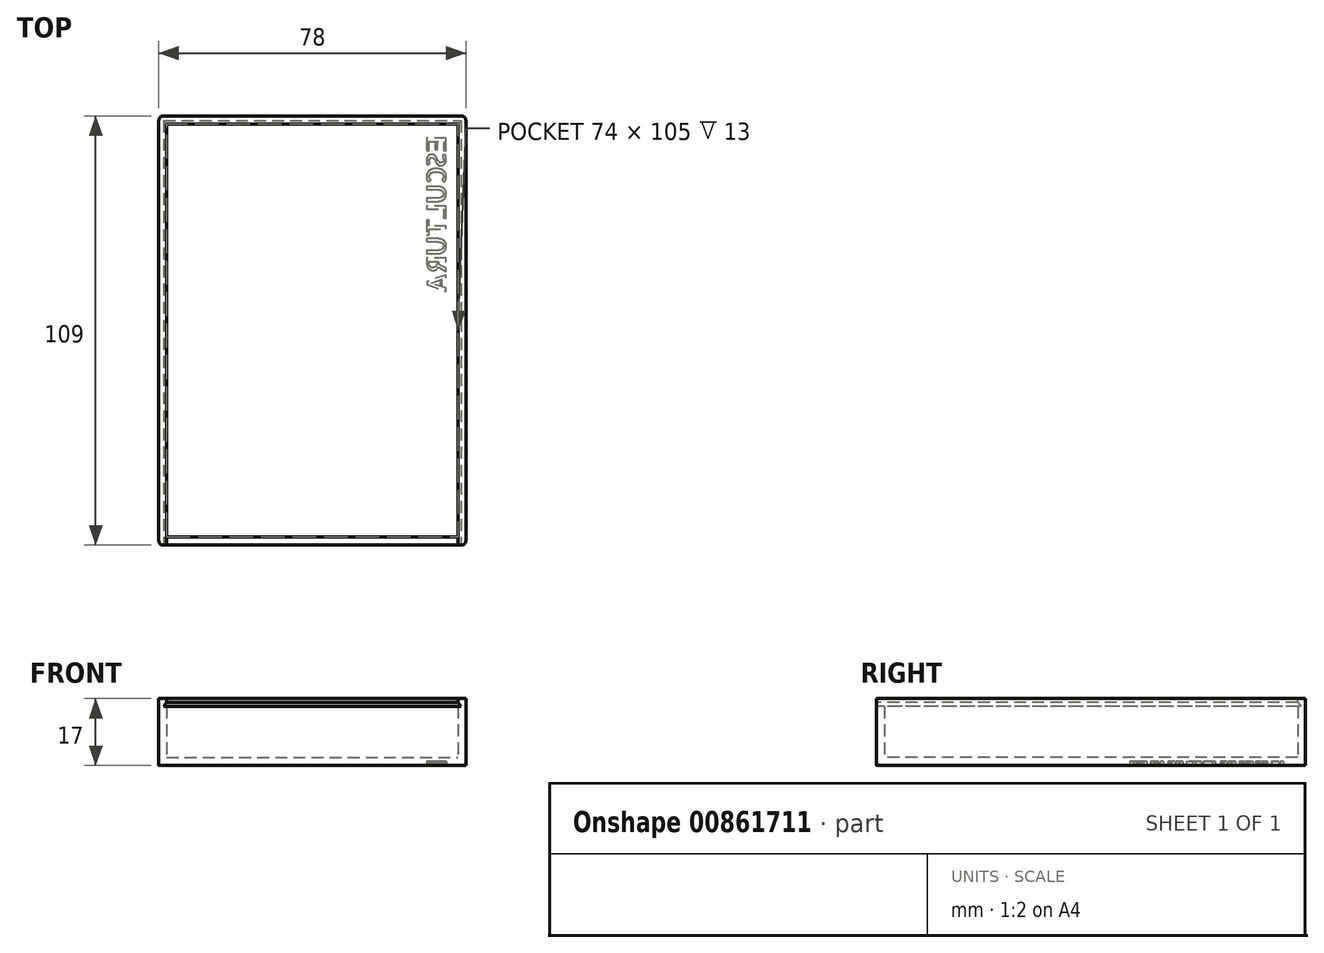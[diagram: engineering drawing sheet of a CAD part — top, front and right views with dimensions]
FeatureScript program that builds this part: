
annotation { "Feature Type Name" : "Feature", "Feature Type Description" : "" }
export const myFeature = defineFeature(function(context is Context, id is Id, definition is map)
    precondition{}
    {
        {
            var Q0;
            Q0=qCreatedBy(makeId("Front.planeOp"),FACE);
            var sketch = newSketch(context, id + "F0", { "sketchPlane" : qUnion([Q0])});
            skLineSegment(sketch, "E0.bottom", {"start": v(0, 0) * mm, "end": v(78, 0) * mm});
            skLineSegment(sketch, "E0.top", {"start": v(0, -15) * mm, "end": v(78, -15) * mm});
            skLineSegment(sketch, "E0.left", {"start": v(0, 0) * mm, "end": v(0, -15) * mm});
            skLineSegment(sketch, "E0.right", {"start": v(78, 0) * mm, "end": v(78, -15) * mm});
            skSolve(sketch);
        }
        {
            var Q0;
            Q0=qSketchRegion(id+"F0",true);
            extrude(context, id + "F1", {"entities" : qUnion([Q0]), "oppositeDirection" : true, "depth" : 109 * mm, "offsetDistance" : 25 * mm});
        }
        {
            var Q0;
            Q0=makeQuery(id+"F1.opExtrude","SWEPT_FACE",FACE,{"disambiguationData":[OSD([sQuery(id+"F0.wireOp",EDGE,"E0.bottom")])]});
            shell(context, id + "F2", {"entities" : qUnion([Q0]), "thickness" : 2 * mm});
        }
        {
            var Q0;
            Q0=makeQuery(id+"F1.opExtrude","CAP_FACE",FACE,{"disambiguationData":[OSD([sQuery(id+"F0.wireOp",EDGE,"E0.bottom"),sQuery(id+"F0.wireOp",EDGE,"E0.top"),sQuery(id+"F0.wireOp",EDGE,"E0.left"),sQuery(id+"F0.wireOp",EDGE,"E0.right")])],"isStart":true});
            var sketch = newSketch(context, id + "F3", { "sketchPlane" : qUnion([Q0])});
            skLineSegment(sketch, "E1", {"start": v(0, 0) * mm, "end": v(0, 2) * mm});
            skLineSegment(sketch, "E2", {"start": v(0, 2) * mm, "end": v(2, 2) * mm});
            skLineSegment(sketch, "E3", {"start": v(2, 2) * mm, "end": v(2, 1) * mm});
            skLineSegment(sketch, "E4", {"start": v(1.2, 0) * mm, "end": v(0, 0) * mm});
            skLineSegment(sketch, "E5", {"start": v(39, -15) * mm, "end": v(39, 0) * mm, "construction": true});
            skLineSegment(sketch, "E6", {"start": v(1.2, 0) * mm, "end": v(2, 1) * mm});
            skLineSegment(sketch, "E7.MirrorCS", {"start": v(76.8, 0) * mm, "end": v(76, 1) * mm});
            skLineSegment(sketch, "E8.MirrorCS", {"start": v(76, 2) * mm, "end": v(76, 1) * mm});
            skLineSegment(sketch, "E9.MirrorCS", {"start": v(76.8, 0) * mm, "end": v(78, 0) * mm});
            skLineSegment(sketch, "E10.MirrorCS", {"start": v(78, 0) * mm, "end": v(78, 2) * mm});
            skLineSegment(sketch, "E11.MirrorCS", {"start": v(78, 2) * mm, "end": v(76, 2) * mm});
            skSolve(sketch);
        }
        {
            var Q0;
            Q0=qSketchRegion(id+"F3",true);
            var Q1;
            Q1=makeQuery(id+"F1.opExtrude","CAP_FACE",FACE,{"disambiguationData":[OSD([sQuery(id+"F0.wireOp",EDGE,"E0.bottom"),sQuery(id+"F0.wireOp",EDGE,"E0.top"),sQuery(id+"F0.wireOp",EDGE,"E0.left"),sQuery(id+"F0.wireOp",EDGE,"E0.right")])],"isStart":false});
            extrude(context, id + "F4", {"entities" : qUnion([Q0]), "operationType" : NewBodyOperationType.ADD, "endBound" : BoundingType.UP_TO_SURFACE, "oppositeDirection" : true, "depth" : 25 * mm, "endBoundEntityFace" : qUnion([Q1]), "offsetDistance" : 25 * mm});
        }
        {
            var Q0;
            Q0=makeQuery(id+"F4.boolean.opBoolean","MERGE",FACE,{"derivedFrom":[makeQuery(id+"F1.opExtrude","SWEPT_FACE",FACE,{"disambiguationData":[OSD([sQuery(id+"F0.wireOp",EDGE,"E0.right")])]}),makeQuery(id+"F4.opExtrude","SWEPT_FACE",FACE,{"disambiguationData":[OSD([sQuery(id+"F3.wireOp",EDGE,"a277ad1f-f057-4d94-afe5-2e5cce70e8dc2.MirrorCS")])]})]});
            var sketch = newSketch(context, id + "F5", { "sketchPlane" : qUnion([Q0])});
            skLineSegment(sketch, "E12", {"start": v(109, 2) * mm, "end": v(107, 2) * mm});
            skLineSegment(sketch, "E13", {"start": v(109, 0) * mm, "end": v(109, 2) * mm});
            skLineSegment(sketch, "E14", {"start": v(109, 0) * mm, "end": v(107.8, 0) * mm});
            skLineSegment(sketch, "E15", {"start": v(107, 2) * mm, "end": v(107, 1) * mm});
            skLineSegment(sketch, "E16", {"start": v(107, 1) * mm, "end": v(107.8, 0) * mm});
            skSolve(sketch);
        }
        {
            var Q0;
            Q0=qSketchRegion(id+"F5",true);
            var Q1;
            Q1=makeQuery(id+"F4.boolean.opBoolean","MERGE",FACE,{"derivedFrom":[makeQuery(id+"F1.opExtrude","SWEPT_FACE",FACE,{"disambiguationData":[OSD([sQuery(id+"F0.wireOp",EDGE,"E0.left")])]}),makeQuery(id+"F4.opExtrude","SWEPT_FACE",FACE,{"disambiguationData":[OSD([sQuery(id+"F3.wireOp",EDGE,"E1")])]})]});
            extrude(context, id + "F6", {"entities" : qUnion([Q0]), "operationType" : NewBodyOperationType.ADD, "endBound" : BoundingType.UP_TO_SURFACE, "oppositeDirection" : true, "depth" : 25 * mm, "endBoundEntityFace" : qUnion([Q1]), "offsetDistance" : 25 * mm});
        }
        {
            var Q0;
            Q0=makeQuery(id+"F4.boolean.opBoolean","MERGE",EDGE,{"derivedFrom":[makeQuery(id+"F1.opExtrude","CAP_EDGE",EDGE,{"disambiguationData":[OSD([sQuery(id+"F0.wireOp",EDGE,"E0.right")])],"isStart":true}),makeQuery(id+"F4.opExtrude","CAP_EDGE",EDGE,{"disambiguationData":[OSD([sQuery(id+"F3.wireOp",EDGE,"a277ad1f-f057-4d94-afe5-2e5cce70e8dc2.MirrorCS")])],"isStart":true})]});
            var Q1;
            {var subQ0=sQuery(id+"F0.wireOp",EDGE,"E0.right");Q1=makeQuery(id+"F4.boolean.opBoolean","MERGE",EDGE,{"derivedFrom":[makeQuery(id+"F1.opExtrude","CAP_EDGE",EDGE,{"disambiguationData":[OSD([subQ0])],"isStart":false}),makeQuery(id+"F4.opExtrude","TWEAK_EDGE",EDGE,{"derivedFrom":[makeQuery(id+"F1.opExtrude","CAP_FACE",FACE,{"disambiguationData":[OSD([sQuery(id+"F0.wireOp",EDGE,"E0.bottom"),sQuery(id+"F0.wireOp",EDGE,"E0.top"),sQuery(id+"F0.wireOp",EDGE,"E0.left"),subQ0])],"isStart":false}),makeQuery(id+"F3.imprint","IMPRINT",EDGE,{"derivedFrom":sQuery(id+"F3.wireOp",EDGE,"a277ad1f-f057-4d94-afe5-2e5cce70e8dc2.MirrorCS")})]})]});}
            var Q2;
            {var subQ0=sQuery(id+"F0.wireOp",EDGE,"E0.left");Q2=makeQuery(id+"F4.boolean.opBoolean","MERGE",EDGE,{"derivedFrom":[makeQuery(id+"F1.opExtrude","CAP_EDGE",EDGE,{"disambiguationData":[OSD([subQ0])],"isStart":false}),makeQuery(id+"F4.opExtrude","TWEAK_EDGE",EDGE,{"derivedFrom":[makeQuery(id+"F1.opExtrude","CAP_FACE",FACE,{"disambiguationData":[OSD([sQuery(id+"F0.wireOp",EDGE,"E0.bottom"),sQuery(id+"F0.wireOp",EDGE,"E0.top"),subQ0,sQuery(id+"F0.wireOp",EDGE,"E0.right")])],"isStart":false}),makeQuery(id+"F3.imprint","IMPRINT",EDGE,{"derivedFrom":sQuery(id+"F3.wireOp",EDGE,"E1")})]})]});}
            var Q3;
            Q3=makeQuery(id+"F4.boolean.opBoolean","MERGE",EDGE,{"derivedFrom":[makeQuery(id+"F1.opExtrude","CAP_EDGE",EDGE,{"disambiguationData":[OSD([sQuery(id+"F0.wireOp",EDGE,"E0.left")])],"isStart":true}),makeQuery(id+"F4.opExtrude","CAP_EDGE",EDGE,{"disambiguationData":[OSD([sQuery(id+"F3.wireOp",EDGE,"E1")])],"isStart":true})]});
            fillet(context, id + "F7", {"entities" : qUnion([Q0, Q1, Q2, Q3]), "radius" : 1.2 * mm, "tangentPropagation" : true, "rho" : 0.5, "crossSection" : FilletCrossSection.CONIC, "allowEdgeOverflow" : false});
        }
        {
            var Q0;
            Q0=makeQuery(id+"F1.opExtrude","SWEPT_FACE",FACE,{"disambiguationData":[OSD([sQuery(id+"F0.wireOp",EDGE,"E0.top")])]});
            var sketch = newSketch(context, id + "F8", { "sketchPlane" : qUnion([Q0])});
            skText(sketch, "E17", { "text": "ESCULTURA", "fontName": "AllertaStencil-Regular.ttf"});
            const initialGuessF8  = {"E17": [0.073, -0.104, 0, 1, 0.00493]};
            skSetInitialGuess(sketch, initialGuessF8);
            skSolve(sketch);
        }
        {
            var Q0;
            Q0=qSketchRegion(id+"F8",true);
            extrude(context, id + "F9", {"entities" : qUnion([Q0]), "operationType" : NewBodyOperationType.REMOVE, "oppositeDirection" : true, "depth" : 1 * mm, "offsetDistance" : 25 * mm});
        }
    });
